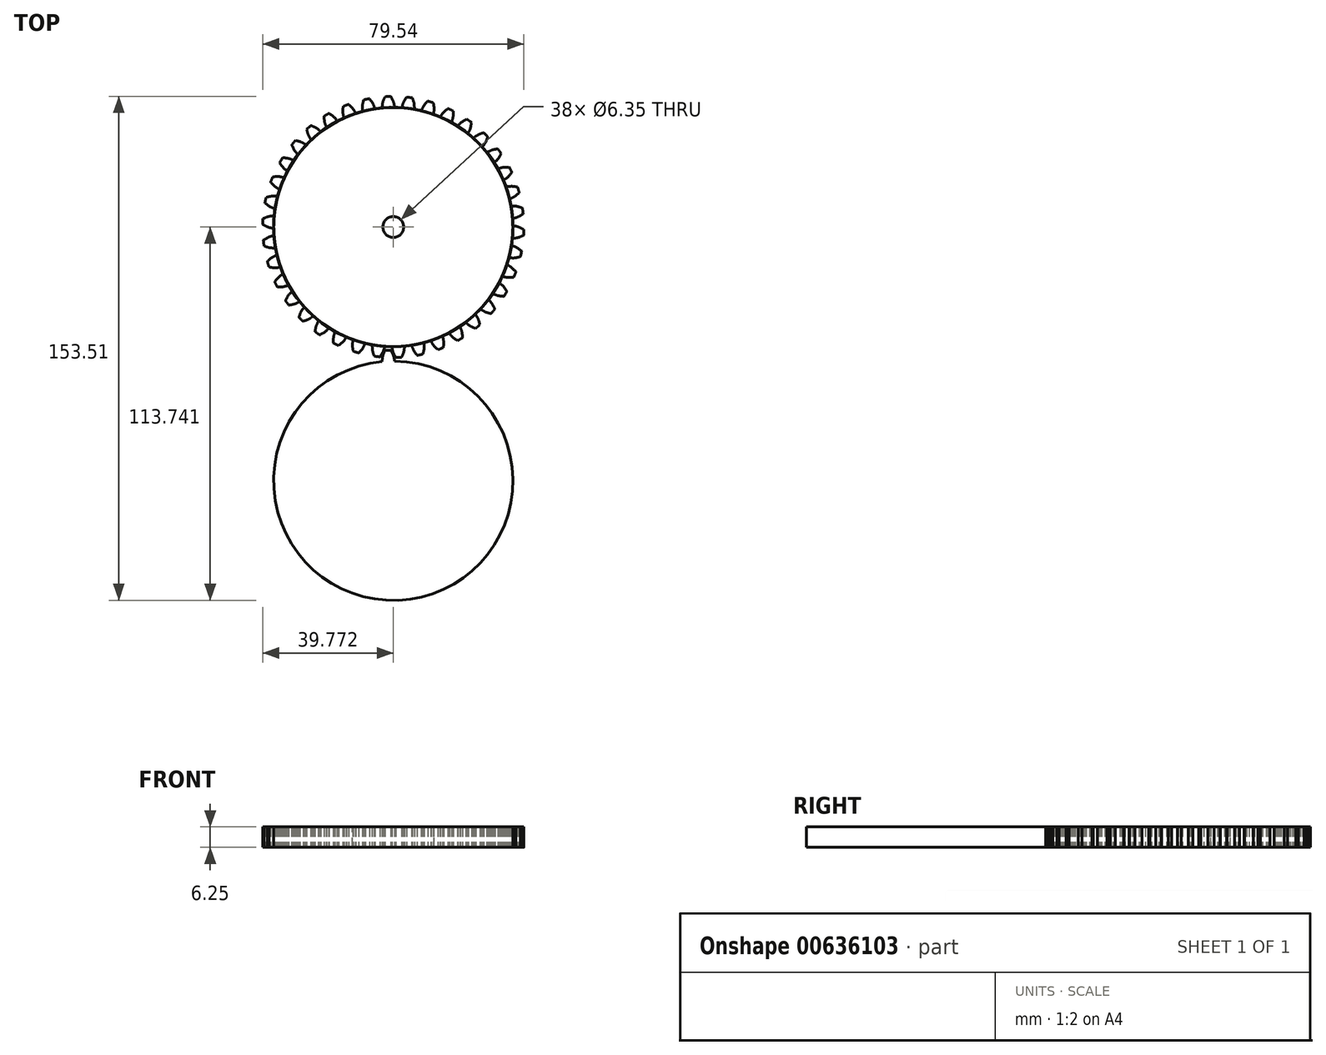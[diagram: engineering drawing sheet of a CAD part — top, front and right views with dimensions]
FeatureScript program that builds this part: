
annotation { "Feature Type Name" : "Feature", "Feature Type Description" : "" }
export const myFeature = defineFeature(function(context is Context, id is Id, definition is map)
    precondition{}
    {
        {
            var Q0;
            Q0=qCreatedBy(makeId("Top.planeOp"),FACE);
            var sketch = newSketch(context, id + "F0", { "sketchPlane" : qUnion([Q0])});
            skCircle(sketch, "E0", {"center": v(0, 0) * mm, "radius": 38.1 * mm, "construction": true});
            skLineSegment(sketch, "E1", {"start": v(0, 0) * mm, "end": v(0, 54.47) * mm, "construction": true});
            skLineSegment(sketch, "E2", {"start": v(-40.8, 38.1) * mm, "end": v(45.04, 38.1) * mm, "construction": true});
            skLineSegment(sketch, "E3", {"start": v(-12.24, 33.64) * mm, "end": v(18.8, 44.94) * mm, "construction": true});
            skLineSegment(sketch, "E4", {"start": v(0, 0) * mm, "end": v(-12.24, 33.64) * mm, "construction": true});
            skCircle(sketch, "E5", {"center": v(0, 0) * mm, "radius": 35.8 * mm, "construction": true});
            skPoint(sketch, "E6", {"position": v(-12.24, 33.64) * mm});
            skPoint(sketch, "E7", {"position": v(0, 38.1) * mm});
            skPoint(sketch, "E8", {"position": v(-16.8, 31.61) * mm});
            skLineSegment(sketch, "E9", {"start": v(-16.8, 31.61) * mm, "end": v(-0.9, 40.1) * mm, "construction": true});
            skArc(sketch, "E10", {"start": v(-7.44, 35.02) * mm, "mid": v(-9.87, 34.42) * mm, "end": v(-12.24, 33.64) * mm});
            skArc(sketch, "E11", {"start": v(-12.24, 33.64) * mm, "mid": v(-14.56, 32.7) * mm, "end": v(-16.8, 31.61) * mm});
            skLineSegment(sketch, "E12", {"start": v(-7.44, 35.02) * mm, "end": v(0.41, 36.69) * mm, "construction": true});
            skLineSegment(sketch, "E13", {"start": v(0, 38.1) * mm, "end": v(0, 0) * mm, "construction": true});
            skLineSegment(sketch, "E14", {"start": v(0.41, 36.69) * mm, "end": v(0.43, 36.44) * mm});
            skArc(sketch, "E15.trimOffspring", {"start": v(0, 36.44) * mm, "mid": v(0, 36.44) * mm, "end": v(0, 36.44) * mm});
            skLineSegment(sketch, "E16", {"start": v(0, 0) * mm, "end": v(-1.9, 46.38) * mm, "construction": true});
            skLineSegment(sketch, "E17.0.MirrorCS", {"start": v(5.36, 0.33) * mm, "end": v(1.52, 46.59) * mm, "construction": true});
            skLineSegment(sketch, "E18.0.MirrorCS", {"start": v(-3.43, 36.53) * mm, "end": v(-3.42, 36.28) * mm});
            skArc(sketch, "E19.converted", {"start": v(-3.42, 36.28) * mm, "mid": v(1.5, -36.41) * mm, "end": v(0.43, 36.44) * mm});
            skLineSegment(sketch, "E20", {"start": v(-3.42, 36.28) * mm, "end": v(-3.42, 36.28) * mm});
            skLineSegment(sketch, "E21", {"start": v(0.43, 36.44) * mm, "end": v(0.43, 36.44) * mm});
            skArc(sketch, "E22.trimOffspring", {"start": v(0.43, 36.44) * mm, "mid": v(-1.5, 36.41) * mm, "end": v(-3.42, 36.28) * mm});
            skArc(sketch, "E23.0", {"start": v(-0.74, 39.77) * mm, "mid": v(-1.64, 39.74) * mm, "end": v(-2.53, 39.7) * mm});
            skFitSpline(sketch, "E24.trimOffspring", {"points": [v(-2.4, 40.03) * mm, v(-3.13, 37.97) * mm, v(-3.43, 36.53) * mm], "startDerivative": vector(-1.5, -3.87) * mm, "endDerivative": vector(-0.5, -3.06) * mm});
            skFitSpline(sketch, "E25.trimOffspring", {"points": [v(-0.9, 40.1) * mm, v(0, 38.1) * mm, v(0.41, 36.69) * mm], "startDerivative": vector(1.82, -3.74) * mm, "endDerivative": vector(0.75, -3.01) * mm});
            skPoint(sketch, "E26.start.orphan", {"position": v(-0.86, 40.02) * mm});
            skPoint(sketch, "E27.trimOffspring.end.orphan", {"position": v(-2.43, 39.95) * mm});
            skCircle(sketch, "E28", {"center": v(0, 0) * mm, "radius": 3.17 * mm});
            skSolve(sketch);
        }
        {
            var Q0;
            Q0=qCreatedBy(makeId("Top.planeOp"),FACE);
            var sketch = newSketch(context, id + "F1", { "sketchPlane" : qUnion([Q0])});
            skFitSpline(sketch, "E29.0", {"points": [v(-2.4, 40.03) * mm, v(-2.68, 39.32) * mm, v(-3.18, 38.02) * mm, v(-3.35, 37) * mm, v(-3.43, 36.53) * mm]});
            skFitSpline(sketch, "E30.0", {"points": [v(-0.9, 40.1) * mm, v(-0.56, 39.4) * mm, v(0.05, 38.15) * mm, v(0.3, 37.14) * mm, v(0.41, 36.69) * mm]});
            skLineSegment(sketch, "E30.1", {"start": v(0.41, 36.69) * mm, "end": v(0.43, 36.44) * mm});
            skLineSegment(sketch, "E30.2", {"start": v(-3.43, 36.53) * mm, "end": v(-3.42, 36.28) * mm});
            skArc(sketch, "E30.3", {"start": v(-0.74, 39.77) * mm, "mid": v(-1.64, 39.74) * mm, "end": v(-2.53, 39.7) * mm});
            skArc(sketch, "E31.0", {"start": v(-3.42, 36.28) * mm, "mid": v(1.5, -36.41) * mm, "end": v(0.43, 36.44) * mm});
            skSolve(sketch);
        }
        {
            var Q0;
            Q0=makeQuery(id+"F1.imprint","IMPRINT",FACE,{"disambiguationData":[TD([[makeQuery(id+"F1.imprint","IMPRINT",EDGE,{"derivedFrom":sQuery(id+"F1.wireOp",EDGE,"E29.0")}),1.0]])]});
            extrude(context, id + "F2", {"entities" : qUnion([Q0]), "depth" : 25 / 4 * mm});
        }
        {
            var Q0;
            Q0=makeQuery(id+"F2.opExtrude","CAP_FACE",FACE,{"disambiguationData":[OSD([sQuery(id+"F1.wireOp",EDGE,"E29.0"),sQuery(id+"F1.wireOp",EDGE,"E30.0"),sQuery(id+"F1.wireOp",EDGE,"E30.1"),sQuery(id+"F1.wireOp",EDGE,"E30.2"),sQuery(id+"F1.wireOp",EDGE,"E30.3"),sQuery(id+"F1.wireOp",EDGE,"E31.0")])],"isStart":false});
            var Q1;
            Q1=makeQuery(id+"F2.opExtrude","SWEPT_BODY",BODY,{"disambiguationData":[OSD([sQuery(id+"F1.wireOp",EDGE,"E29.0"),sQuery(id+"F1.wireOp",EDGE,"E30.0"),sQuery(id+"F1.wireOp",EDGE,"E30.1"),sQuery(id+"F1.wireOp",EDGE,"E30.2"),sQuery(id+"F1.wireOp",EDGE,"E30.3"),sQuery(id+"F1.wireOp",EDGE,"E31.0")])]});
            var Q2;
            Q2=sQuery(id+"F1.wireOp",EDGE,"E31.0");
            circularPattern(context, id + "F3", {"entities" : qUnion([Q1]), "axis" : qUnion([Q2]), "angle" : 360 * degree, "instanceCount" : 38, "equalSpace" : true});
        }
        {
            var Q0;
            Q0=makeQuery(id+"F0.imprint","IMPRINT",FACE,{"disambiguationData":[TD([[makeQuery(id+"F0.imprint","IMPRINT",EDGE,{"derivedFrom":sQuery(id+"F0.wireOp",EDGE,"E28")}),1.0]])]});
            extrude(context, id + "F4", {"entities" : qUnion([Q0]), "operationType" : NewBodyOperationType.REMOVE, "depth" : 25 * mm});
        }
        {
            var Q0;
            Q0=qCreatedBy(makeId("Top.planeOp"),FACE);
            var sketch = newSketch(context, id + "F5", { "sketchPlane" : qUnion([Q0])});
            skFitSpline(sketch, "E32.0", {"points": [v(-2.4, -37.27) * mm, v(-2.68, -37.98) * mm, v(-3.18, -39.29) * mm, v(-3.35, -40.31) * mm, v(-3.43, -40.77) * mm]});
            skFitSpline(sketch, "E33.0", {"points": [v(-0.9, -37.21) * mm, v(-0.56, -37.9) * mm, v(0.05, -39.15) * mm, v(0.3, -40.16) * mm, v(0.41, -40.61) * mm]});
            skLineSegment(sketch, "E33.1", {"start": v(0.41, -40.61) * mm, "end": v(0.43, -40.86) * mm});
            skLineSegment(sketch, "E33.2", {"start": v(-3.43, -40.77) * mm, "end": v(-3.42, -41.02) * mm});
            skArc(sketch, "E33.3", {"start": v(-0.74, -37.53) * mm, "mid": v(-1.64, -37.56) * mm, "end": v(-2.53, -37.6) * mm});
            skArc(sketch, "E34.0", {"start": v(-3.42, -41.02) * mm, "mid": v(1.5, -113.71) * mm, "end": v(0.43, -40.86) * mm});
            skSolve(sketch);
        }
        {
            var Q0;
            Q0=makeQuery(id+"F5.imprint","IMPRINT",FACE,{"disambiguationData":[TD([[makeQuery(id+"F5.imprint","IMPRINT",EDGE,{"derivedFrom":sQuery(id+"F5.wireOp",EDGE,"E32.0")}),1.0]])]});
            extrude(context, id + "F6", {"entities" : qUnion([Q0]), "depth" : 6.25 * mm, "offsetDistance" : 25 * mm});
        }
    });
